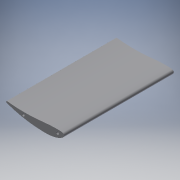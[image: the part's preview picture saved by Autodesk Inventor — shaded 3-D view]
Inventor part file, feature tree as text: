
AUTODESK INVENTOR PART (.ipt)
format: ipt  version: 2018 (Build 220112000, 112)  size: 156,672 bytes
history: native  units: mm
features: other x6, extrude x3, sketch x3, reference x3, projected_geometry x1
ambient origin geometry x8: Origin, YZ Plane, XZ Plane, XY Plane, X Axis, Y Axis, Z Axis, Center Point
bodies: Body1 (feature_tree)
feature tree (16):
  extrude  "押し出し1"  Depth=250.0mm TaperAngle=0.0deg
  extrude  "押し出し2"  Depth=225.0mm TaperAngle=0.0deg
  other  "作業平面2"
  extrude  "押し出し3"  Depth=140.0mm
  other  "ソリッド13"
  sketch  "スケッチ1"
  projected_geometry  "投影ループ1"
  sketch  "スケッチ2"
  other  "作業平面1"
  sketch  "スケッチ3"
  reference  "参照1"
  reference  "参照2"
  reference  "参照3"
  other  "<userpath>\Documents\Inventor\Aero\KS-15\Fr.wing\Fr.wing_assy.iam"
  other  "Fr.wing_assy.iam"
  other  "endplate_ver2:1"
